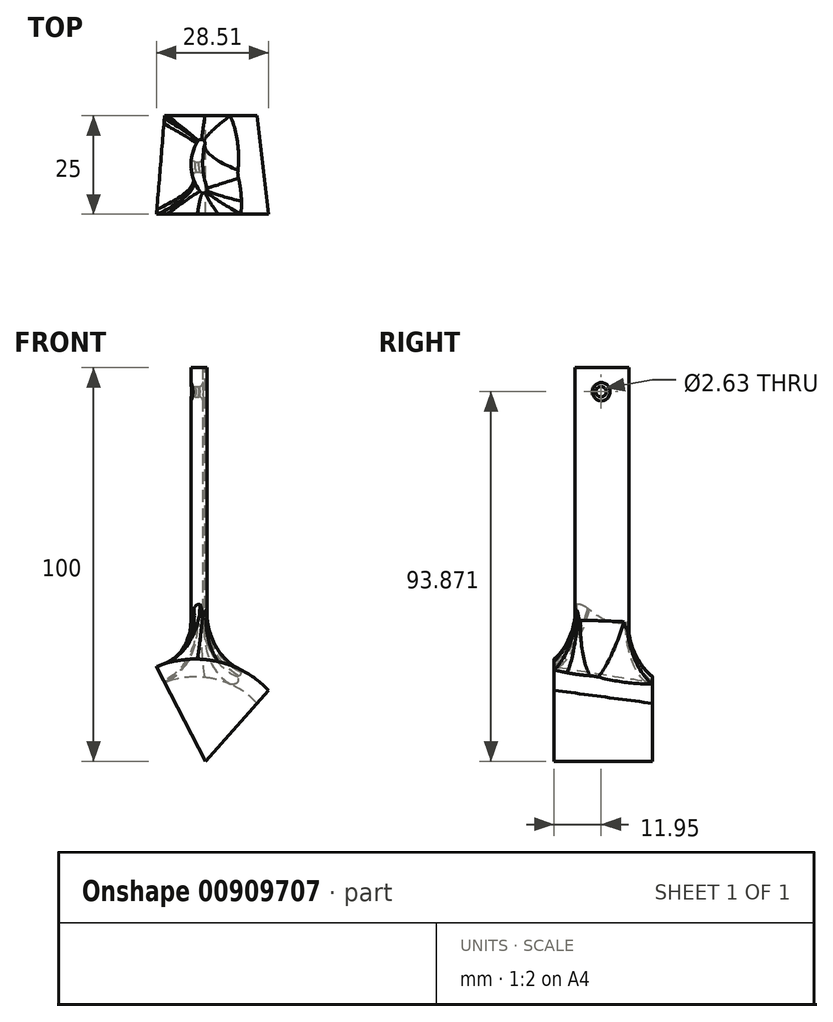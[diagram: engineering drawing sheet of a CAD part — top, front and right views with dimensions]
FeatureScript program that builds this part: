
annotation { "Feature Type Name" : "Feature", "Feature Type Description" : "" }
export const myFeature = defineFeature(function(context is Context, id is Id, definition is map)
    precondition{}
    {
        {
            var Q0;
            Q0=qCreatedBy(makeId("Front.planeOp"),FACE);
            var sketch = newSketch(context, id + "F0", { "sketchPlane" : qUnion([Q0])});
            skCircle(sketch, "E0", {"center": v(-2.69, 0) * mm, "radius": 21.54 * mm});
            skSolve(sketch);
        }
        {
            var Q0;
            Q0 = qSketchRegion(id + "F0", true);
            extrude(context, id + "F1", {"entities" : qUnion([Q0]), "depth" : 25 * mm, "offsetDistance" : 25 * mm, "hasDraft" : true, "draftAngle" : 10 * degree});
        }
        {
            var Q0;
            Q0=qCreatedBy(makeId("Top.planeOp"),FACE);
            var sketch = newSketch(context, id + "F2", { "sketchPlane" : qUnion([Q0])});
            skArc(sketch, "E1", {"start": v(1.31, -3.06) * mm, "mid": v(-3.75, -12.98) * mm, "end": v(2.24, -22.37) * mm});
            skArc(sketch, "E2", {"start": v(1.31, -3.06) * mm, "mid": v(-0.77, -12.83) * mm, "end": v(2.24, -22.37) * mm});
            skSolve(sketch);
        }
        {
            var Q0;
            Q0 = qSketchRegion(id + "F2", true);
            extrude(context, id + "F3", {"entities" : qUnion([Q0]), "operationType" : NewBodyOperationType.ADD, "depth" : 100 * mm, "offsetDistance" : 25 * mm});
        }
        {
            var Q0;
            Q0=qCreatedBy(makeId("Front.planeOp"),FACE);
            var sketch = newSketch(context, id + "F4", { "sketchPlane" : qUnion([Q0])});
            skLineSegment(sketch, "E3", {"start": v(0, 0) * mm, "end": v(-15.22, 29.17) * mm});
            skLineSegment(sketch, "E4", {"start": v(-15.22, 29.17) * mm, "end": v(-39.91, -0.9) * mm});
            skLineSegment(sketch, "E5", {"start": v(-39.91, -0.9) * mm, "end": v(-24.32, -27.83) * mm});
            skLineSegment(sketch, "E6", {"start": v(-24.32, -27.83) * mm, "end": v(38.25, -25.97) * mm});
            skLineSegment(sketch, "E7", {"start": v(38.25, -25.97) * mm, "end": v(26.56, 29.92) * mm});
            skLineSegment(sketch, "E8", {"start": v(26.56, 29.92) * mm, "end": v(0, 0) * mm});
            skSolve(sketch);
        }
        {
            var Q0;
            Q0 = qSketchRegion(id + "F4", true);
            extrude(context, id + "F5", {"entities" : qUnion([Q0]), "operationType" : NewBodyOperationType.REMOVE, "endBound" : BoundingType.THROUGH_ALL, "depth" : 25 * mm, "offsetDistance" : 25 * mm});
        }
        {
            var Q0;
            {var subQ0=sQuery(id+"F2.wireOp",EDGE,"E2");var subQ1=sQuery(id+"F2.wireOp",EDGE,"E1");Q0=makeQuery(id+"F3.opExtrude","SWEPT_EDGE",EDGE,{"disambiguationData":[OSD([subQ1,subQ0]),TDD([makeQuery(id+"F2.imprint","INTERSECT",VERTEX,{"disambiguationData":[OD(0.0)],"derivedFrom":[subQ1,subQ0]})])]});}
            var Q1;
            {var subQ0=sQuery(id+"F2.wireOp",EDGE,"E2");var subQ1=sQuery(id+"F2.wireOp",EDGE,"E1");Q1=makeQuery(id+"F3.opExtrude","SWEPT_EDGE",EDGE,{"disambiguationData":[OSD([subQ1,subQ0]),TDD([makeQuery(id+"F2.imprint","INTERSECT",VERTEX,{"disambiguationData":[OD(1.0)],"derivedFrom":[subQ1,subQ0]})])]});}
            fillet(context, id + "F6", {"entities" : qUnion([Q0, Q1]), "radius" : 1 * mm, "tangentPropagation" : true, "allowEdgeOverflow" : false});
        }
        {
            var Q0;
            Q0=makeQuery(id+"F3.boolean.opBoolean","INTERSECT",EDGE,{"derivedFrom":[makeQuery(id+"F1.opExtrude","SWEPT_FACE",FACE,{"disambiguationData":[OSD([sQuery(id+"F0.wireOp",EDGE,"E0")])]}),makeQuery(id+"F3.opExtrude","SWEPT_FACE",FACE,{"disambiguationData":[OSD([sQuery(id+"F2.wireOp",EDGE,"E2")])]})]});
            fillet(context, id + "F7", {"entities" : qUnion([Q0]), "radius" : 16 * mm, "tangentPropagation" : true, "allowEdgeOverflow" : false});
        }
        {
            var Q0;
            Q0=qCreatedBy(makeId("Right.planeOp"),FACE);
            var sketch = newSketch(context, id + "F8", { "sketchPlane" : qUnion([Q0])});
            skCircle(sketch, "E9", {"center": v(-13.05, 93.87) * mm, "radius": 1.31 * mm});
            skSolve(sketch);
        }
        {
            var Q0;
            Q0 = qSketchRegion(id + "F8", true);
            extrude(context, id + "F9", {"entities" : qUnion([Q0]), "operationType" : NewBodyOperationType.REMOVE, "endBound" : BoundingType.THROUGH_ALL, "oppositeDirection" : true, "depth" : 25 * mm, "offsetDistance" : 25 * mm});
        }
        {
            var Q0;
            Q0=makeQuery(id+"F9.boolean.opBoolean","COPY",FACE,{"derivedFrom":makeQuery(id+"F9.opExtrude","SWEPT_FACE",FACE,{"disambiguationData":[OSD([sQuery(id+"F8.wireOp",EDGE,"E9")])]})});
            fillet(context, id + "F10", {"entities" : qUnion([Q0]), "radius" : 1 * mm, "tangentPropagation" : true, "allowEdgeOverflow" : false});
        }
    });
